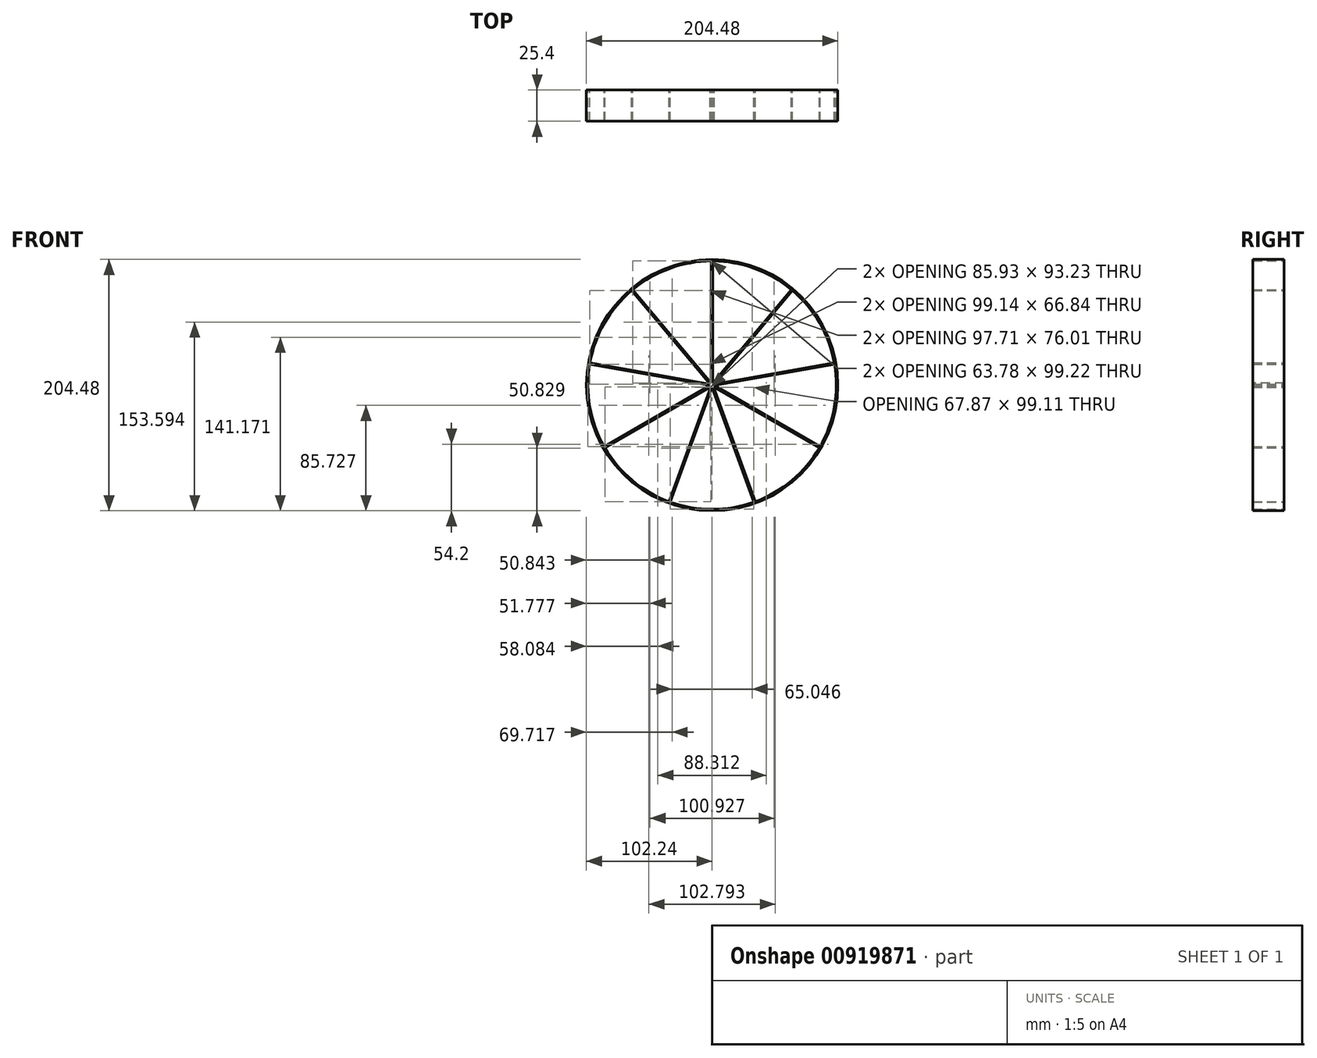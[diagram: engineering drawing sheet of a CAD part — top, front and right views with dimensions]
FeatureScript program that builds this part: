
annotation { "Feature Type Name" : "Feature", "Feature Type Description" : "" }
export const myFeature = defineFeature(function(context is Context, id is Id, definition is map)
    precondition{}
    {
        {
            var Q0;
            Q0=qCreatedBy(makeId("Front.planeOp"),FACE);
            var sketch = newSketch(context, id + "F0", { "sketchPlane" : qUnion([Q0])});
            skCircle(sketch, "E0", {"center": v(0, 0) * mm, "radius": 101.6 * mm, "construction": true});
            skLineSegment(sketch, "E1", {"start": v(0, 0) * mm, "end": v(0, 101.6) * mm, "construction": true});
            skLineSegment(sketch, "E2.1.0", {"start": v(0, 0) * mm, "end": v(-65.3, 77.83) * mm, "construction": true});
            skLineSegment(sketch, "E2.2.0", {"start": v(0, 0) * mm, "end": v(-100.06, 17.64) * mm, "construction": true});
            skLineSegment(sketch, "E2.3.0", {"start": v(0, 0) * mm, "end": v(-87.99, -50.8) * mm, "construction": true});
            skLineSegment(sketch, "E2.4.0", {"start": v(0, 0) * mm, "end": v(-34.75, -95.47) * mm, "construction": true});
            skLineSegment(sketch, "E2.5.0", {"start": v(0, 0) * mm, "end": v(34.75, -95.47) * mm, "construction": true});
            skLineSegment(sketch, "E2.6.0", {"start": v(0, 0) * mm, "end": v(87.99, -50.8) * mm, "construction": true});
            skLineSegment(sketch, "E2.7.0", {"start": v(0, 0) * mm, "end": v(100.06, 17.64) * mm, "construction": true});
            skLineSegment(sketch, "E2.8.0", {"start": v(0, 0) * mm, "end": v(65.3, 77.83) * mm, "construction": true});
            skCircle(sketch, "E3.0", {"center": v(0, 0) * mm, "radius": 102.23 * mm});
            skCircle(sketch, "E4.0", {"center": v(0, 0) * mm, "radius": 100.97 * mm});
            skSolve(sketch);
        }
        {
            var Q0;
            Q0=makeQuery(id+"F0.imprint","IMPRINT",FACE,{"disambiguationData":[TD([[makeQuery(id+"F0.imprint","IMPRINT",EDGE,{"derivedFrom":sQuery(id+"F0.wireOp",EDGE,"E3.0")}),1.0]])]});
            var Q1;
            Q1=sQuery(id+"F0.wireOp",EDGE,"E4.0");
            var Q2;
            Q2=sQuery(id+"F0.wireOp",EDGE,"E3.0");
            extrude(context, id + "F1", {"entities" : qUnion([Q0]), "surfaceEntities" : qUnion([Q1, Q2]), "depth" : 25.4 * mm, "offsetDistance" : 25.4 * mm});
        }
        {
            var Q0;
            Q0=qCreatedBy(makeId("Front.planeOp"),FACE);
            var sketch = newSketch(context, id + "F2", { "sketchPlane" : qUnion([Q0])});
            skLineSegment(sketch, "E5", {"start": v(0, 0) * mm, "end": v(0, 101.04) * mm, "construction": true});
            skLineSegment(sketch, "E6.0", {"start": v(0.64, 0) * mm, "end": v(0.64, 101.04) * mm});
            skLineSegment(sketch, "E7.0", {"start": v(-0.64, 0) * mm, "end": v(-0.64, 101.04) * mm});
            skLineSegment(sketch, "E8", {"start": v(-0.64, 0) * mm, "end": v(0.64, 0) * mm});
            skLineSegment(sketch, "E9", {"start": v(-0.64, 101.04) * mm, "end": v(0.64, 101.04) * mm});
            skSolve(sketch);
        }
        {
            var Q0;
            Q0 = qSketchRegion(id + "F2", true);
            extrude(context, id + "F3", {"entities" : qUnion([Q0]), "depth" : 25.4 * mm, "offsetDistance" : 25.4 * mm});
        }
        {
            var Q0;
            Q0=qCreatedBy(makeId("Top.planeOp"),FACE);
            var sketch = newSketch(context, id + "F4", { "sketchPlane" : qUnion([Q0])});
            skLineSegment(sketch, "E10", {"start": v(0, -21.7) * mm, "end": v(0, 31.28) * mm});
            skSolve(sketch);
        }
        {
            var Q0;
            Q0=makeQuery(id+"F3.opExtrude","SWEPT_BODY",BODY,{"disambiguationData":[OSD([sQuery(id+"F2.wireOp",EDGE,"E6.0"),sQuery(id+"F2.wireOp",EDGE,"E7.0"),sQuery(id+"F2.wireOp",EDGE,"E8"),sQuery(id+"F2.wireOp",EDGE,"E9")])]});
            var Q1;
            Q1=sQuery(id+"F4.wireOp",EDGE,"E10");
            circularPattern(context, id + "F5", {"operationType" : NewBodyOperationType.ADD, "entities" : qUnion([Q0]), "axis" : qUnion([Q1]), "angle" : 360 * degree, "instanceCount" : 9, "equalSpace" : true});
        }
    });
